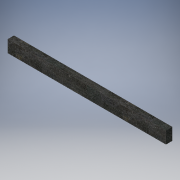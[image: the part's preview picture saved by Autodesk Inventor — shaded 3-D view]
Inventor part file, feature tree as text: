
AUTODESK INVENTOR PART (.ipt)
format: ipt  version: 2019 (Build 230136000, 136)  size: 102,912 bytes
history: native  units: mm
features: extrude x1, sketch x1
ambient origin geometry x8: Origin, YZ Plane, XZ Plane, XY Plane, X Axis, Y Axis, Z Axis, Center Point
bodies: Solid1 (feature_tree)
feature tree (2):
  extrude  "Extrusion1"  Depth=20.0mm
  sketch  "Sketch1"  dims[d0=260.0mm d1=20.0mm d2=217.645673mm d3=10.0mm d4=10.0mm d5=0.0mm]
